# Revit family: O29201001_Sanitario Montecarlo Advance Redondo
name_source: partatom
category: Plumbing Fixtures
units: mm (PartAtom-declared; Revit-internal decimal feet)

## family parameters
Always vertical = Yes
Cut with Voids When Loaded = No
Host = Floor
OmniClass Number = 23.31.19.17
OmniClass Title = Toilets With Tank
Part Type = Normal
Room Calculation Point = No
Round Connector Dimension = Use Diameter
Shared = No

## types (1)
- O29201001_Sanitario Montecarlo Advance Redondo
    Alto = 630 mm  [stored 2.06693 ft]
    Ancho = 410 mm  [stored 1.34514 ft]
    Capacidad de descarga = 500 g
    Colección = Montecarlo Advance
    Consumo de agua = 4.6 lt
    Creado por = IDD
    Description = Disfruta de la tecnología MaxiClean que este sanitario te ofrece, el cual permite un mejor lavado de la taza, reduciendo gérmenes y bacterias. Una pieza que no puede faltar en tu baño.
    Espejo de agua = 20.5 x 23.5 cm
    Fabricante = Corona
    Fecha de creación = 13/08/2020
    Garantía = Garantia completa para siempre en la porcelana
    Garantías de otros componentes = 5 años en grifería tanque y asiento
    Incluye = Taza-tanque, válvula de entrada, válvula de salida, botón de descarga tipo push, asiento sanitario cierre lento
    Longitud = 730 mm  [stored 2.39501 ft]
    Línea = Montecarlo Advance
    Material = Corona_Porcelana_Sanitaria
    Peso Bruto aprox = 37,6 kg
    Peso Neto aprox = 31,1 kg
    Presión de agua = 20 - 80 PSI
    Sistema de descarga = Botón tipo push
    Tecnologías = MaxiClean
    Tipo de asiento = Cierre lento
    Tipo de instalación = A piso
    Tipo de sifón = Oculto
    Tipo de tanque = Taza-tanque
    Tipo de válvula = Válvula de descarga sencilla
    URL = https://corona.co
    Uso = Residencial

note: [stored X ft] marks values corroborated as IEEE doubles in the binary element streams (Revit-internal decimal feet)

## geometry (parser evidence)
native form markers: Sweep x12
no freeform markers — native parametric forms only
